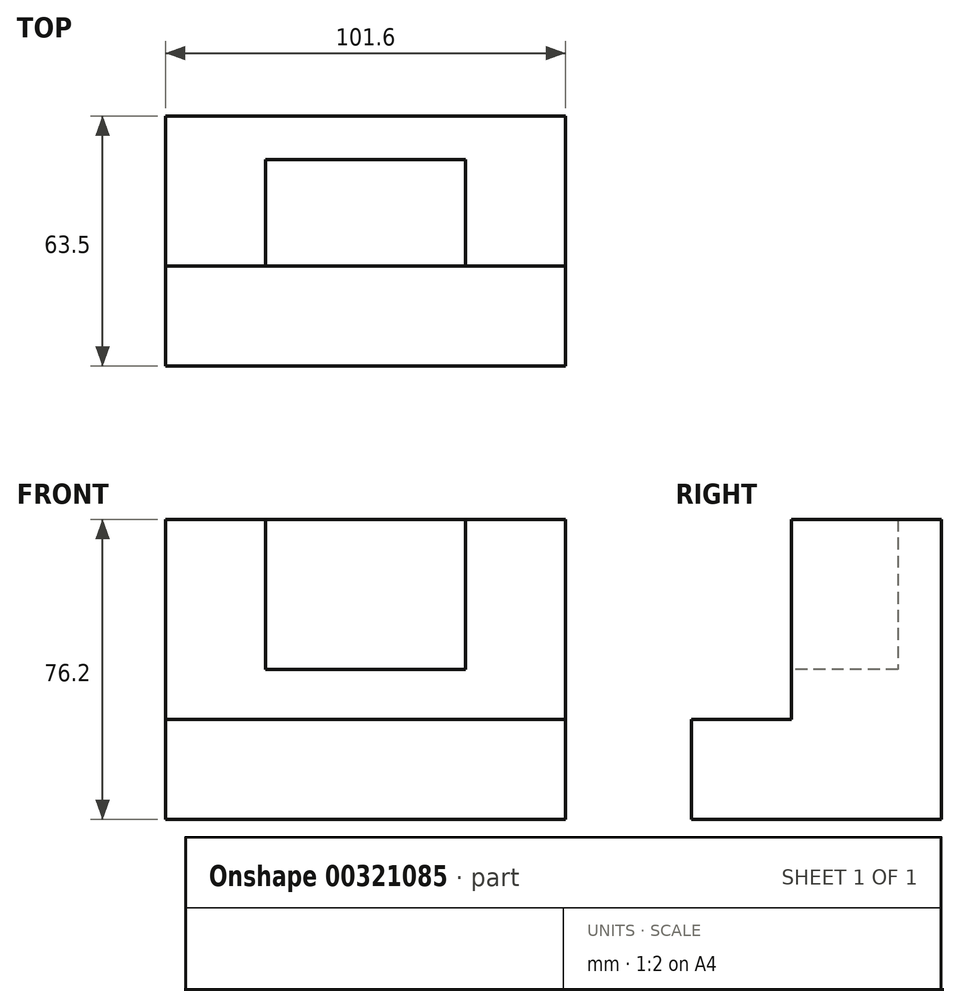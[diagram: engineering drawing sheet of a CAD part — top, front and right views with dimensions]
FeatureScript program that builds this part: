
annotation { "Feature Type Name" : "Feature", "Feature Type Description" : "" }
export const myFeature = defineFeature(function(context is Context, id is Id, definition is map)
    precondition{}
    {
        {
            var Q0;
            Q0=qCreatedBy(makeId("Right.planeOp"),FACE);
            var sketch = newSketch(context, id + "F0", { "sketchPlane" : qUnion([Q0])});
            skLineSegment(sketch, "E0", {"start": v(-27.03, 44.18) * mm, "end": v(11.07, 44.18) * mm});
            skLineSegment(sketch, "E1", {"start": v(11.07, 44.18) * mm, "end": v(11.07, -32.02) * mm});
            skLineSegment(sketch, "E2", {"start": v(11.07, -32.02) * mm, "end": v(-52.43, -32.02) * mm});
            skLineSegment(sketch, "E3", {"start": v(-52.43, -32.02) * mm, "end": v(-52.43, -6.62) * mm});
            skLineSegment(sketch, "E4", {"start": v(-52.43, -6.62) * mm, "end": v(-27.03, -6.62) * mm});
            skLineSegment(sketch, "E5", {"start": v(-27.03, -6.62) * mm, "end": v(-27.03, 44.18) * mm});
            skSolve(sketch);
        }
        {
            var Q0;
            Q0=makeQuery(id+"F0.imprint","IMPRINT",FACE,{"disambiguationData":[TD([[makeQuery(id+"F0.imprint","IMPRINT",EDGE,{"derivedFrom":sQuery(id+"F0.wireOp",EDGE,"E0")}),-1.0]])]});
            extrude(context, id + "F1", {"entities" : qUnion([Q0]), "depth" : 101.6 * mm});
        }
        {
            var Q0;
            Q0=makeQuery(id+"F1.opExtrude","SWEPT_FACE",FACE,{"disambiguationData":[OSD([sQuery(id+"F0.wireOp",EDGE,"E5")])]});
            var sketch = newSketch(context, id + "F2", { "sketchPlane" : qUnion([Q0])});
            skLineSegment(sketch, "E6", {"start": v(50.8, 44.18) * mm, "end": v(76.2, 44.18) * mm});
            skLineSegment(sketch, "E7", {"start": v(50.8, 44.18) * mm, "end": v(25.4, 44.18) * mm});
            skLineSegment(sketch, "E8.bottom", {"start": v(25.4, 44.18) * mm, "end": v(76.2, 44.18) * mm});
            skLineSegment(sketch, "E8.top", {"start": v(25.4, 6.08) * mm, "end": v(76.2, 6.08) * mm});
            skLineSegment(sketch, "E8.left", {"start": v(25.4, 44.18) * mm, "end": v(25.4, 6.08) * mm});
            skLineSegment(sketch, "E8.right", {"start": v(76.2, 44.18) * mm, "end": v(76.2, 6.08) * mm});
            skSolve(sketch);
        }
        {
            var Q0;
            Q0 = qSketchRegion(id + "F2", true);
            var Q1;
            Q1=makeQuery(id+"F2.imprint","IMPRINT",FACE,{"disambiguationData":[TD([[makeQuery(id+"F2.imprint","IMPRINT",EDGE,{"derivedFrom":sQuery(id+"F2.wireOp",EDGE,"E8.bottom")}),1.0]])]});
            extrude(context, id + "F3", {"entities" : qUnion([Q0, Q1]), "operationType" : NewBodyOperationType.REMOVE, "oppositeDirection" : true, "depth" : 130.05 * mm});
        }
        {
            var Q0;
            Q0=makeQuery(id+"F3.boolean.opBoolean","COPY",FACE,{"derivedFrom":makeQuery(id+"F3.opExtrude","SWEPT_FACE",FACE,{"disambiguationData":[OSD([sQuery(id+"F2.wireOp",EDGE,"E8.right")])]})});
            var sketch = newSketch(context, id + "F4", { "sketchPlane" : qUnion([Q0])});
            skLineSegment(sketch, "E9.bottom", {"start": v(-11.07, 44.18) * mm, "end": v(0, 44.18) * mm});
            skLineSegment(sketch, "E9.top", {"start": v(-11.07, 6.08) * mm, "end": v(0, 6.08) * mm});
            skLineSegment(sketch, "E9.left", {"start": v(-11.07, 44.18) * mm, "end": v(-11.07, 6.08) * mm});
            skLineSegment(sketch, "E9.right", {"start": v(0, 44.18) * mm, "end": v(0, 6.08) * mm});
            skSolve(sketch);
        }
        {
            var Q0;
            Q0=makeQuery(id+"F4.imprint","IMPRINT",FACE,{"disambiguationData":[TD([[makeQuery(id+"F4.imprint","IMPRINT",EDGE,{"derivedFrom":sQuery(id+"F4.wireOp",EDGE,"E9.bottom")}),-1.0]])]});
            extrude(context, id + "F5", {"entities" : qUnion([Q0]), "operationType" : NewBodyOperationType.ADD, "depth" : 60.2 * mm});
        }
    });
